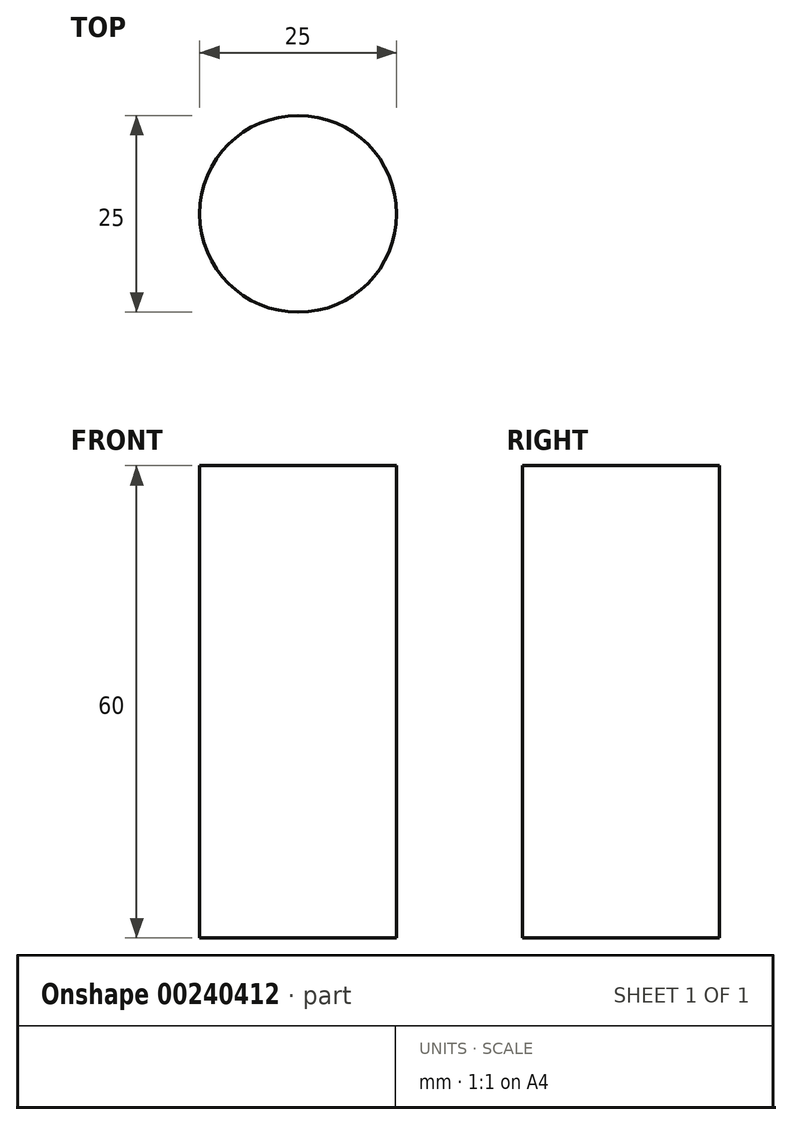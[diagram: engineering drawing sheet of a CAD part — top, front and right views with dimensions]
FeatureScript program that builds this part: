
annotation { "Feature Type Name" : "Feature", "Feature Type Description" : "" }
export const myFeature = defineFeature(function(context is Context, id is Id, definition is map)
    precondition{}
    {
        {
            var Q0;
            Q0=qCreatedBy(makeId("Top.planeOp"),FACE);
            var sketch = newSketch(context, id + "F0", { "sketchPlane" : qUnion([Q0])});
            skCircle(sketch, "E0", {"center": v(0, 0) * mm, "radius": 12.5 * mm});
            skSolve(sketch);
        }
        {
            var Q0;
            Q0=qSketchRegion(id+"F0",true);
            extrude(context, id + "F1", {"entities" : qUnion([Q0]), "depth" : 60 * mm});
        }
    });
